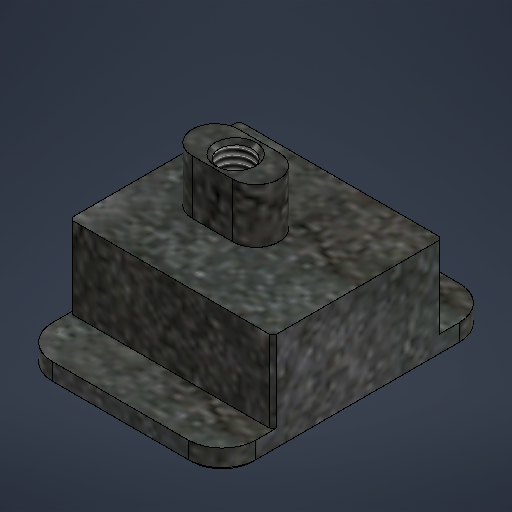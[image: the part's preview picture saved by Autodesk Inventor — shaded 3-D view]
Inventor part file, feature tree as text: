
AUTODESK INVENTOR PART (.ipt)
format: ipt  version: 2025.3 (Build 293356000, 356)  size: 423,936 bytes
history: native  units: mm
features: extrude x4, sketch x2, hole x1, fillet x1, chamfer x1
ambient origin geometry x8: Origin, YZ Plane, XZ Plane, XY Plane, X Axis, Y Axis, Z Axis, Center Point
bodies: Solid1 (feature_tree)
feature tree (9):
  sketch  "Sketch1"  dims[d0=40.0mm d1=30.0mm]
  extrude  "Extrusion1"  Depth=30.0mm
  extrude  "Extrusion2"  Depth=6.8mm
  extrude  "Extrusion5"  Depth=23.0mm TaperAngle=0.0deg
  extrude  "Extrusion6"  Depth=8.0mm TaperAngle=0.0deg
  hole  "Hole1"  [1 undecoded]
  fillet  "Fillet1"  Radius=0.5mm
  chamfer  "Chamfer1"  Distance=3.0mm
  sketch  "Sketch3"  dims[d2=6.0mm d3=6.8mm d4=23.0mm d5=0.0mm d6=8.0mm d7=0.0mm d8=4.917mm d9=10.0mm d10=6.0mm d11=2.0mm d12=90.0deg d13=15.0mm d14=0.0mm d15=5.0mm d16=0.5mm d17=2.0mm d18=45.0deg d19=3.0mm d29=15.0mm d30=10.0mm d31=0.0mm d35=25.0mm d36=20.0mm d37=0.0mm]
note: 1 required parameter value undecoded (feature->parameter linkage not recoverable at this tier; creation-order binding heuristic only, values carry confidence <= 0.55)
